# Revit family: 0030338 Sylvania Lighting Fixture START Downlight 225 IP44 DALI 2350Lm 830
name_source: partatom
category: Lighting Fixtures
revit_build: Autodesk Revit 2016 (Build: 20150220_1215(x64)
units: mm (PartAtom-declared; Revit-internal decimal feet)

## family parameters
Cut with Voids When Loaded = No
Host = Face
Light Source = Yes
OmniClass Number = 23.80.70.00
OmniClass Title = Lighting
Part Type = Normal
Room Calculation Point = No
Round Connector Dimension = Use Diameter
Shared = No

## types (1)
- 0030338 ST DOWNLIGHT 225 IP44 DALI 2350LM 830
    Apparent Load = 24 VA
    Assembly Code = D5020200
    AssetType = Fixed
    ClassificationName = Uniclass2015
    ClassificationValue = EF_70_80
    Color Filter = 16777215
    Cost = 0 $
    Default Elevation = 1219 mm
    DiameterRecess_SYL = 216 mm  [stored 0.708661 ft]
    DiameterTop_SYL = 105 mm  [stored 0.344488 ft]
    Diameter_SYL = 240 mm  [stored 0.787402 ft]
    Dimming Lamp Color Temperature Shift = <None>
    DimmingControlOptions = Dimmable
    DocumentationLiterature = http://www.sylvania-lighting.com
    DurationUnit = hours
    ElectricShockClassification = Class II
    Emit Shape Visible in Rendering = No
    Emit from Circle Diameter = 200 mm  [stored 0.656168 ft]
    ExpectedLife = 50000
    Height_SYL = 62 mm  [stored 0.203412 ft]
    IfcExportAs = IfcLightFixtureType
    IfcExportType = IfcLightFixtureType
    ImpactProtectionIndex = IK07
    IngressProtection = IP20/44
    InputNominalFrequency = 50/60 Hz
    InputVoltage = 220-240V~
    Keynote = 16500
    L_SYL = No
    Lamp = LED
    LampColourRenderingIndex = 80
    LampColourTemperature = 3000 K
    LampMacAdamStep = 5
    LampNominalLuminous = 2330 lm
    LampsType = LED
    LightOutputRatio = 100
    LuminousEfficacy = 97.09 lm/W
    M_SYL = No
    Manufacturer = Feilo Sylvania
    ManufacturerName = Feilo Sylvania
    Material = aluminium housing, polycarbonate diffuser
    Material_1_FEILO = Trim-Sylvania-STARTDownlight-White
    Material_2_FEILO = Diffuser-Sylvania-STARTDownlight
    Material_3_FEILO = Top-Sylvania-STARTDownlight
    Material_4_FEILO = LED-Sylvania-STARTDownlight
    Model = START Downlight 225 IP44 DALI 2350Lm 830
    ModelNumber = 0030338
    ModelReference = START Downlight 225 IP44 DALI 2350Lm 830
    Name = START Downlight 225 IP44 DALI 2350Lm 830
    NominalDepth = 240 mm  [stored 0.787402 ft]
    NominalHeight = 65 mm
    NominalLength = 240 mm  [stored 0.787402 ft]
    Photometric Web File = 0030338.ies
    PowerConsumption = 24 W
    PowerFactor = 0.9
    RadiusTop_SYL = 120 mm  [stored 0.393701 ft]
    S_SYL = No
    Tilt Angle = -90.00°
    Type Image = <None>
    TypeName = START Downlight 225 IP44 DALI 2350Lm 830
    URL = http://www.sylvania-lighting.com
    Voltage = 230 V
    Weight = 10.26 kg

note: [stored X ft] marks values corroborated as IEEE doubles in the binary element streams (Revit-internal decimal feet)

## geometry (parser evidence)
native form markers: Sweep x3
no freeform markers — native parametric forms only
